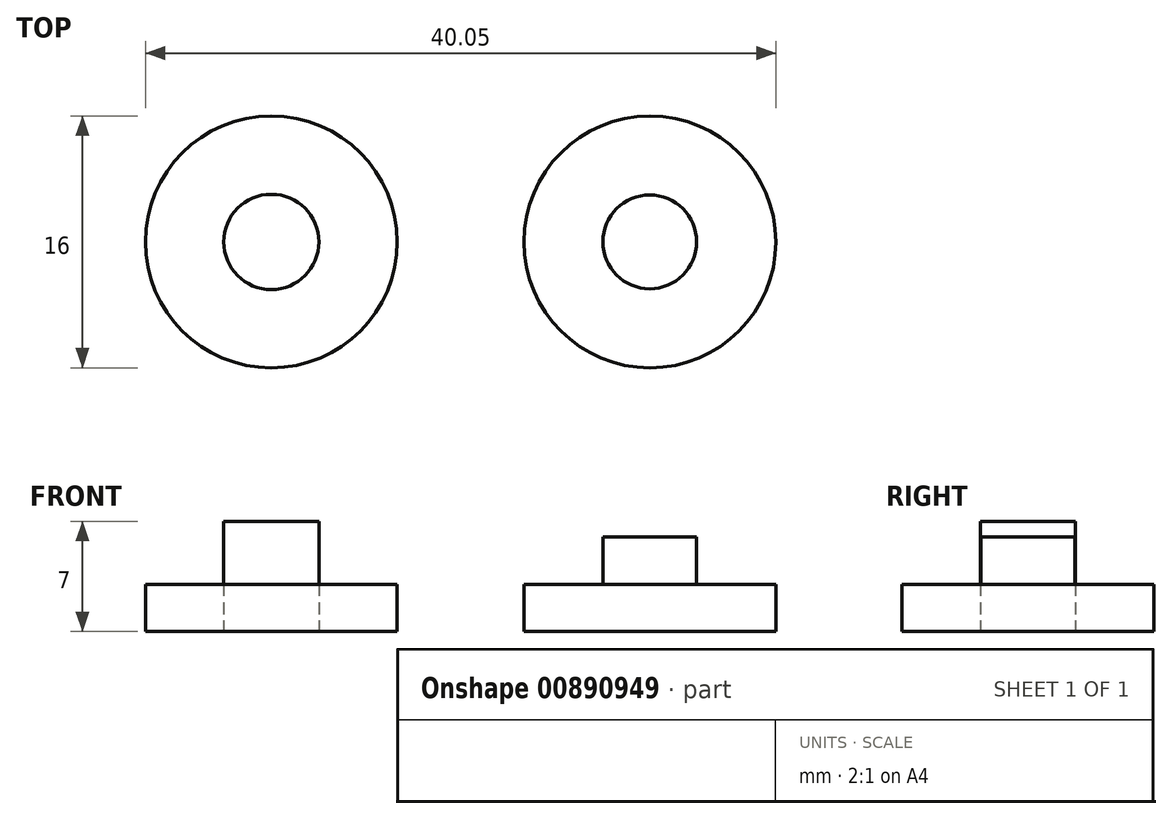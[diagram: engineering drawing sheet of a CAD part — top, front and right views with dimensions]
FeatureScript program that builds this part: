
annotation { "Feature Type Name" : "Feature", "Feature Type Description" : "" }
export const myFeature = defineFeature(function(context is Context, id is Id, definition is map)
    precondition{}
    {
        {
            var Q0;
            Q0=qCreatedBy(makeId("Top.planeOp"),FACE);
            var sketch = newSketch(context, id + "F0", { "sketchPlane" : qUnion([Q0])});
            skCircle(sketch, "E0", {"center": v(0, 0) * mm, "radius": 8 * mm});
            skCircle(sketch, "E1", {"center": v(24.05, 0) * mm, "radius": 8 * mm});
            skSolve(sketch);
        }
        {
            var Q0;
            Q0=qCreatedBy(makeId("Top.planeOp"),FACE);
            var sketch = newSketch(context, id + "F1", { "sketchPlane" : qUnion([Q0])});
            skCircle(sketch, "E2", {"center": v(24.04, 0) * mm, "radius": 2.98 * mm});
            skSolve(sketch);
        }
        {
            var Q0;
            Q0=makeQuery(id+"F0.imprint","IMPRINT",FACE,{"disambiguationData":[TD([[makeQuery(id+"F0.imprint","IMPRINT",EDGE,{"derivedFrom":sQuery(id+"F0.wireOp",EDGE,"E0")}),1.0]])]});
            var sketch = newSketch(context, id + "F2", { "sketchPlane" : qUnion([Q0])});
            skCircle(sketch, "E3", {"center": v(0, 0) * mm, "radius": 3.02 * mm});
            skSolve(sketch);
        }
        {
            var Q0;
            Q0 = qSketchRegion(id + "F0", true);
            extrude(context, id + "F3", {"entities" : qUnion([Q0]), "depth" : 3 * mm, "offsetDistance" : 25 * mm});
        }
        {
            var Q0;
            Q0 = qSketchRegion(id + "F1", true);
            extrude(context, id + "F4", {"entities" : qUnion([Q0]), "operationType" : NewBodyOperationType.ADD, "depth" : 6 * mm, "offsetDistance" : 25 * mm});
        }
        {
            var Q0;
            Q0 = qSketchRegion(id + "F2", true);
            var Q1;
            Q1=sQuery(id+"F2.wireOp",EDGE,"E3");
            extrude(context, id + "F5", {"entities" : qUnion([Q0]), "surfaceEntities" : qUnion([Q1]), "depth" : 7 * mm, "offsetDistance" : 25 * mm});
        }
    });
